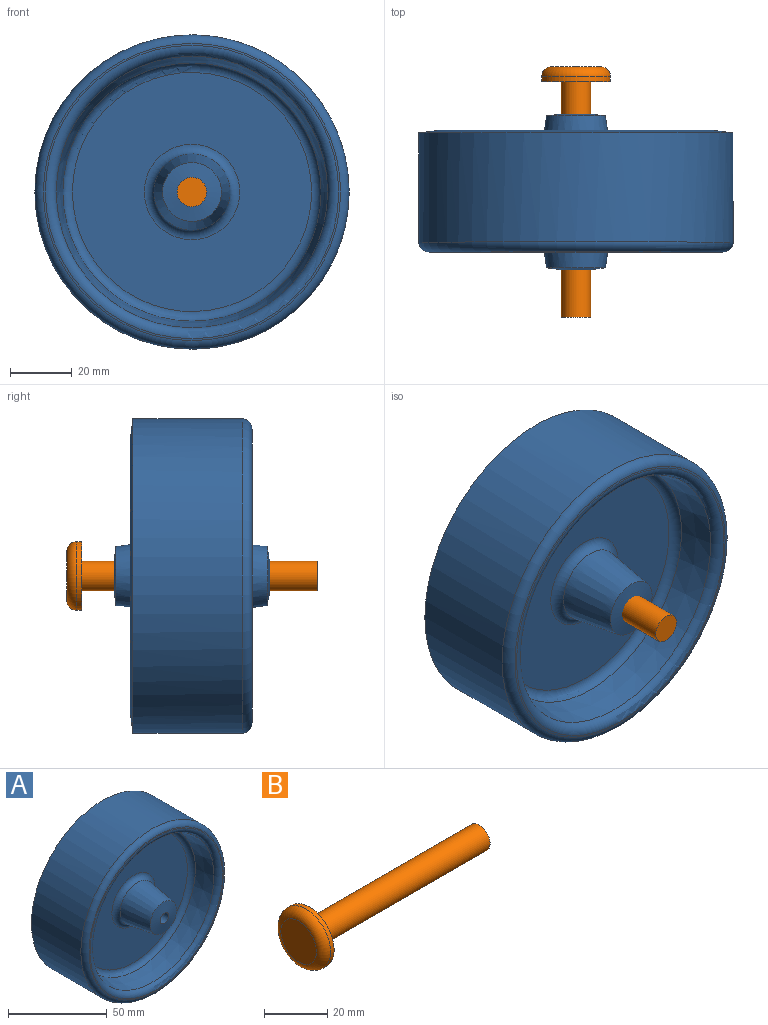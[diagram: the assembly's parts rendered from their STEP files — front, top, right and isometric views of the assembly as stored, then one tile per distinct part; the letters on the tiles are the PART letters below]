
ASSEMBLY  parts=2 mates=1
PART A: 18 faces, bbox 110x50.8x110 mm
  f0: cone r=44.45mm half-angle=82.4deg, axis (0,-1,0), area 1917mm2, adj f1,f15
  f1: cone r=41.77mm half-angle=10.8deg, axis (0,1,0), area 3898mm2, adj f0,f2
  f2: torus R=38.65mm, axis (0,1,0), area 1117.9mm2, adj f1,f3
  f3: plane 77.29x77.29mm, normal (0,1,0), area 3943.3mm2, adj f2,f4
  f4: torus R=15.44mm, axis (0,1,0), area 384.3mm2, adj f3,f5
  f5: cone r=12.3mm half-angle=8.4deg, axis (0,-1,0), area 1294mm2, adj f4,f6
  f6: cone r=3.17mm half-angle=82.4deg, axis (0,-1,0), area 255.6mm2, adj f5,f7
  f7: cylinder r=3.17mm len=50.8mm, axis (0,1,0), area 1013.4mm2, adj f6,f8
  f8: cone r=9.53mm half-angle=82.4deg, axis (0,1,0), area 255.6mm2, adj f7,f9
  f9: cone r=12.3mm half-angle=8.4deg, axis (0,1,0), area 1294mm2, adj f8,f10
  f10: torus R=15.44mm, axis (0,1,0), area 384.3mm2, adj f9,f11
  f11: plane 77.29x77.29mm, normal (0,-1,0), area 3943.3mm2, adj f10,f12
  f12: torus R=38.65mm, axis (0,1,0), area 1117.9mm2, adj f11,f13
  f13: cone r=41.77mm half-angle=10.8deg, axis (0,-1,0), area 3064.1mm2, adj f12,f17
  f14: cone r=50.8mm half-angle=82.4deg, axis (0,1,0), area 186.5mm2, adj f16,f17
  f15: cylinder r=50.8mm len=101.6mm, axis (0,1,0), area 11273.7mm2, adj f0,f16
  f16: torus R=47.62mm, axis (0,-1,0), area 1429.2mm2, adj f14,f15
  f17: torus R=47.01mm, axis (0,-1,0), area 1370.4mm2, adj f13,f14
PART B: 6 faces, bbox 81x24.1x24.1 mm
  f0: plane 22.23x22.23mm, normal (1,0,0), area 316.7mm2, adj f1,f5
  f1: cylinder r=4.76mm len=76.2mm, axis (1,0,0), area 2280.2mm2, adj f0,f2
  f2: plane 9.53x9.53mm, normal (1,0,0), area 71.3mm2, adj f1
  f3: plane 15.88x15.88mm, normal (-1,0,0), area 197.9mm2, adj f4
  f4: torus R=7.94mm, axis (1,0,0), area 312.1mm2, adj f3,f5
  f5: cylinder r=11.11mm len=22.23mm, axis (1,0,0), area 110.8mm2, adj f0,f4
PLACE A t=(-21.33,-35.88,-25.98)mm
PLACE B rot(axis=(0,0,-1),90deg) t=(-86.5,-77.73,-25.98)mm
MATE slider B.f4 <-> A.f8  axis (0,-1,0) through (-55.51,-41.16,-25.98)mm
